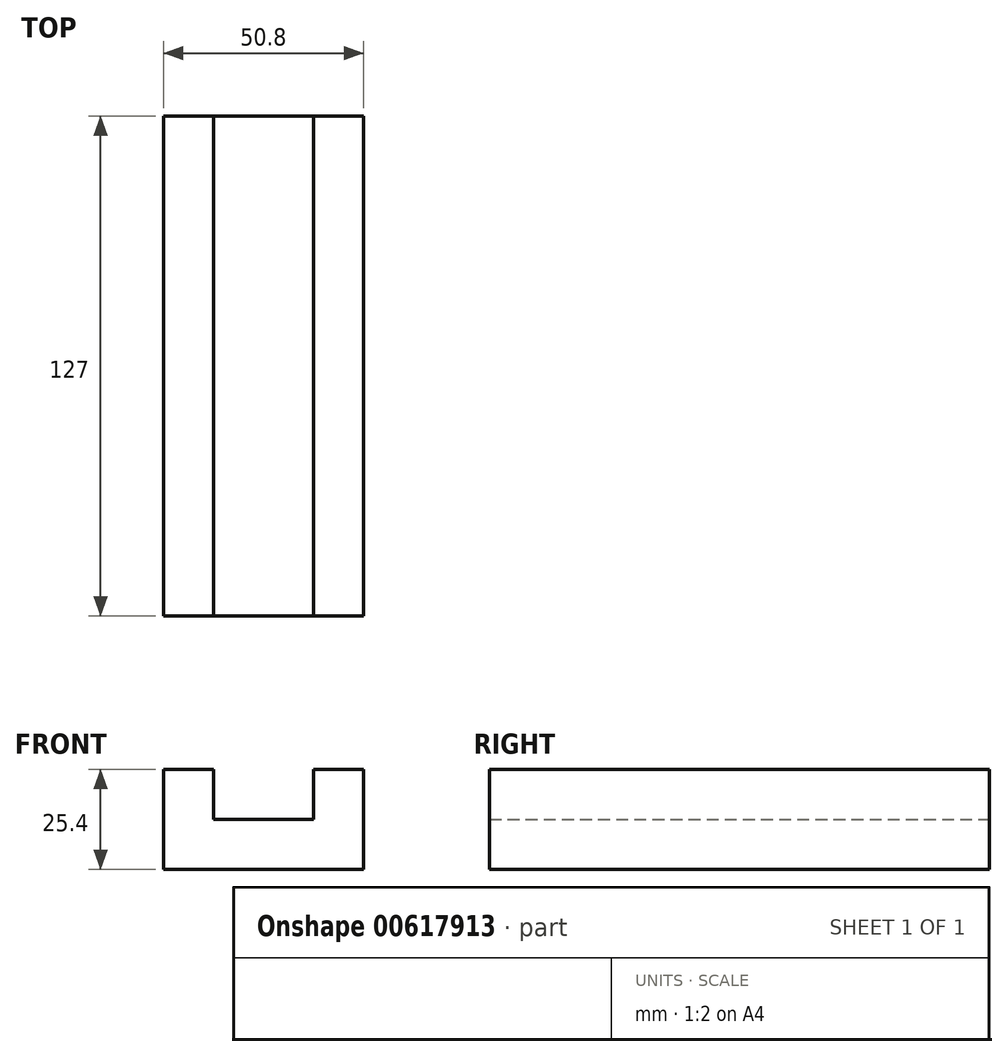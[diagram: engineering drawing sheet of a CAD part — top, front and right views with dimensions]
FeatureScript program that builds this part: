
annotation { "Feature Type Name" : "Feature", "Feature Type Description" : "" }
export const myFeature = defineFeature(function(context is Context, id is Id, definition is map)
    precondition{}
    {
        {
            var Q0;
            Q0=qCreatedBy(makeId("Front.planeOp"),FACE);
            var sketch = newSketch(context, id + "F0", { "sketchPlane" : qUnion([Q0])});
            skLineSegment(sketch, "E0", {"start": v(0, 0) * mm, "end": v(0, 25.4) * mm});
            skLineSegment(sketch, "E1", {"start": v(0, 25.4) * mm, "end": v(12.7, 25.4) * mm});
            skLineSegment(sketch, "E2", {"start": v(12.7, 25.4) * mm, "end": v(12.7, 12.7) * mm});
            skLineSegment(sketch, "E3", {"start": v(12.7, 12.7) * mm, "end": v(38.1, 12.7) * mm});
            skLineSegment(sketch, "E4", {"start": v(38.1, 12.7) * mm, "end": v(38.1, 25.4) * mm});
            skLineSegment(sketch, "E5", {"start": v(38.1, 25.4) * mm, "end": v(50.8, 25.4) * mm});
            skLineSegment(sketch, "E6", {"start": v(50.8, 25.4) * mm, "end": v(50.8, 0) * mm});
            skLineSegment(sketch, "E7", {"start": v(50.8, 0) * mm, "end": v(0, 0) * mm});
            skSolve(sketch);
        }
        {
            var Q0;
            Q0 = qSketchRegion(id + "F0", true);
            extrude(context, id + "F1", {"entities" : qUnion([Q0]), "depth" : 127 * mm, "offsetDistance" : 25.4 * mm});
        }
    });
